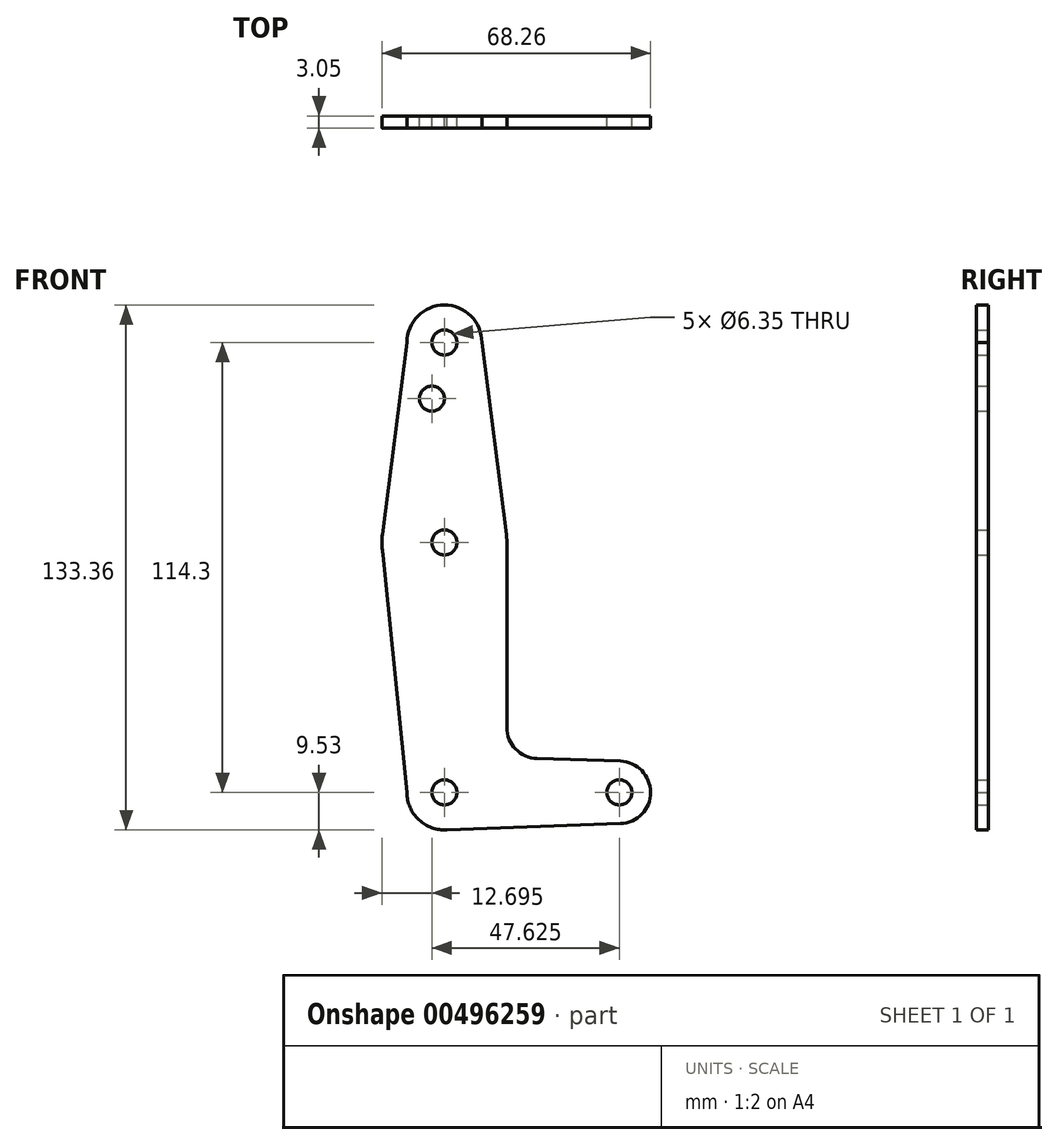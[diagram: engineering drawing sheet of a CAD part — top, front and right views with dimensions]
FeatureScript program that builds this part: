
annotation { "Feature Type Name" : "Feature", "Feature Type Description" : "" }
export const myFeature = defineFeature(function(context is Context, id is Id, definition is map)
    precondition{}
    {
        {
            var Q0;
            Q0=qCreatedBy(makeId("Front.planeOp"),FACE);
            var sketch = newSketch(context, id + "F0", { "sketchPlane" : qUnion([Q0])});
            skLineSegment(sketch, "E0", {"start": v(0, 0) * mm, "end": v(0, 114.3) * mm});
            skLineSegment(sketch, "E1", {"start": v(0, 0) * mm, "end": v(44.45, 0) * mm});
            skCircle(sketch, "E2", {"center": v(0, 114.3) * mm, "radius": 9.53 * mm});
            skCircle(sketch, "E3", {"center": v(44.45, 0) * mm, "radius": 7.94 * mm});
            skLineSegment(sketch, "E4", {"start": v(23.58, 8.58) * mm, "end": v(44.7, 7.93) * mm});
            skCircle(sketch, "E5", {"center": v(0, 114.3) * mm, "radius": 3.18 * mm});
            skCircle(sketch, "E6", {"center": v(-3.18, 100.03) * mm, "radius": 3.18 * mm});
            skCircle(sketch, "E7", {"center": v(0, 63.5) * mm, "radius": 15.88 * mm});
            skLineSegment(sketch, "E8", {"start": v(-9.53, 114.3) * mm, "end": v(-15.75, 65.5) * mm});
            skLineSegment(sketch, "E9", {"start": v(9.53, 114.3) * mm, "end": v(15.75, 65.5) * mm});
            skLineSegment(sketch, "E10", {"start": v(15.88, 63.5) * mm, "end": v(15.88, 16.53) * mm});
            skCircle(sketch, "E11", {"center": v(0, 63.5) * mm, "radius": 3.18 * mm});
            skCircle(sketch, "E12", {"center": v(44.45, 0) * mm, "radius": 3.18 * mm});
            skCircle(sketch, "E13", {"center": v(0, 0) * mm, "radius": 3.18 * mm});
            skArc(sketch, "E14.filletArc", {"start": v(15.88, 16.53) * mm, "mid": v(18.12, 11) * mm, "end": v(23.58, 8.58) * mm});
            skCircle(sketch, "E15", {"center": v(0, 0) * mm, "radius": 9.53 * mm});
            skLineSegment(sketch, "E16", {"start": v(0, -9.53) * mm, "end": v(44.73, -7.93) * mm});
            skLineSegment(sketch, "E17", {"start": v(-15.88, 63.5) * mm, "end": v(-15.57, 60.38) * mm});
            skLineSegment(sketch, "E18", {"start": v(-15.88, 63.5) * mm, "end": v(-9.53, 0) * mm});
            skSolve(sketch);
        }
        {
            var Q0;
            Q0 = qSketchRegion(id + "F0", true);
            var Q1;
            {var subQ0=sQuery(id+"F0.wireOp",EDGE,"E13");var subQ1=sQuery(id+"F0.wireOp",EDGE,"E0");var subQ2=makeQuery(id+"F0.imprint","INTERSECT",VERTEX,{"derivedFrom":[subQ1,subQ0]});Q1=makeQuery(id+"F0.imprint","IMPRINT",FACE,{"disambiguationData":[TD([[makeQuery(id+"F0.imprint","IMPRINT",EDGE,{"disambiguationData":[TD([[subQ2,-1.0]])],"derivedFrom":subQ1}),-1.0]])]});}
            extrude(context, id + "F1", {"entities" : qUnion([Q0, Q1]), "depth" : 3.05 * mm});
        }
    });
